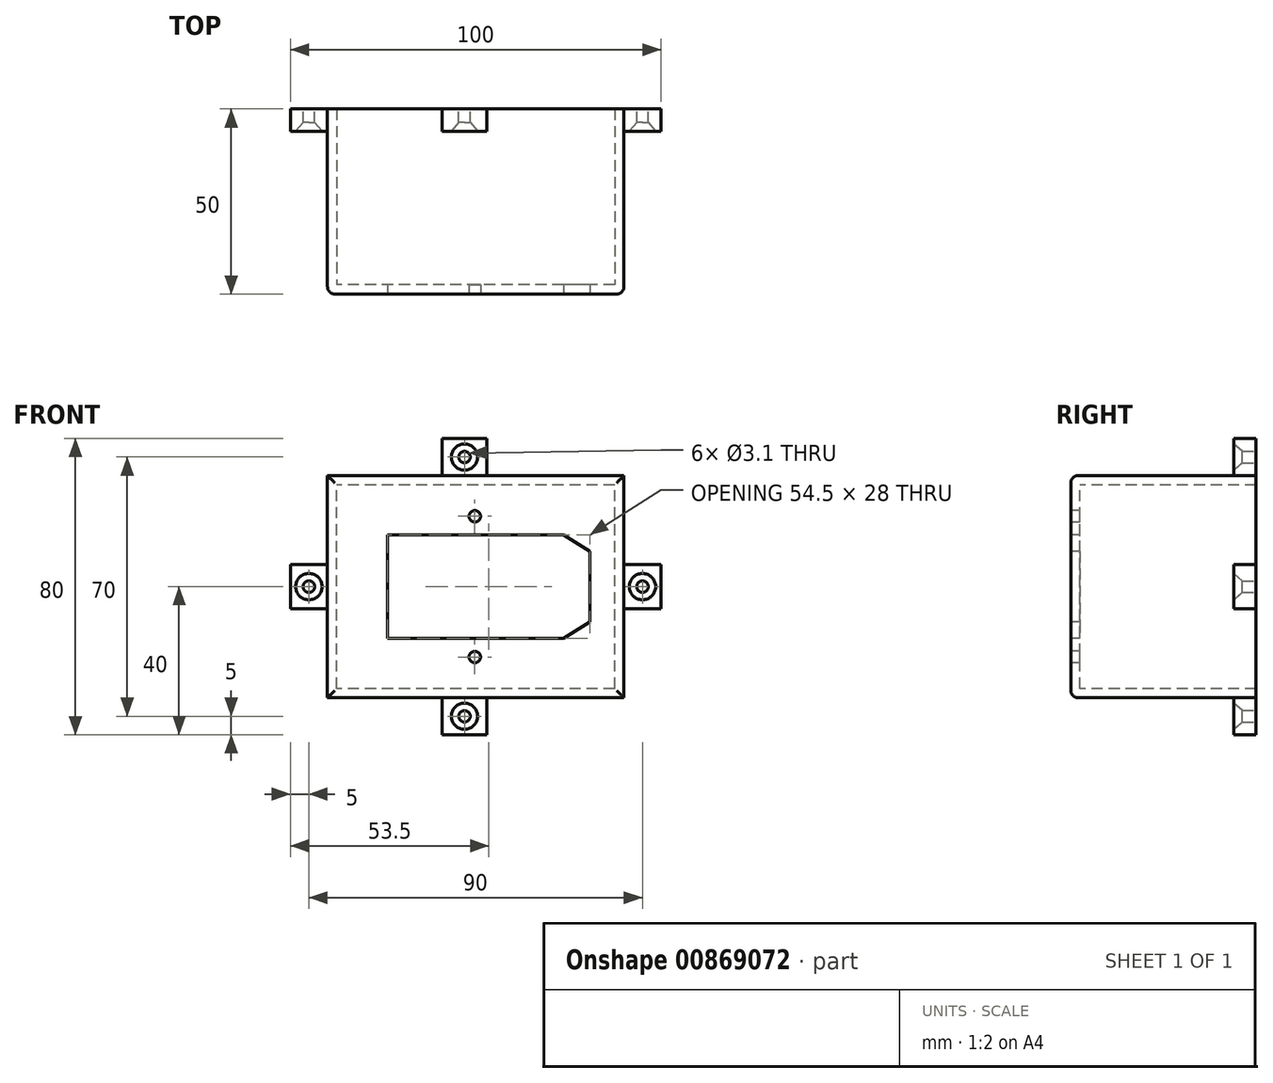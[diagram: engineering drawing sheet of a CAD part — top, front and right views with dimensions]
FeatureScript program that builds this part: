
annotation { "Feature Type Name" : "Feature", "Feature Type Description" : "" }
export const myFeature = defineFeature(function(context is Context, id is Id, definition is map)
    precondition{}
    {
        {
            var Q0;
            Q0=qCreatedBy(makeId("Front.planeOp"),FACE);
            var sketch = newSketch(context, id + "F0", { "sketchPlane" : qUnion([Q0])});
            skLineSegment(sketch, "E0.bottom", {"start": v(40, -30) * mm, "end": v(-40, -30) * mm});
            skLineSegment(sketch, "E0.top", {"start": v(40, 30) * mm, "end": v(-40, 30) * mm});
            skLineSegment(sketch, "E0.left", {"start": v(40, -30) * mm, "end": v(40, 30) * mm});
            skLineSegment(sketch, "E0.right", {"start": v(-40, -30) * mm, "end": v(-40, 30) * mm});
            skPoint(sketch, "E0.middle", {"position": v(0, 0) * mm});
            skLineSegment(sketch, "E1.bottom", {"start": v(23.75, -14) * mm, "end": v(-23.75, -14) * mm});
            skLineSegment(sketch, "E1.top", {"start": v(23.75, 14) * mm, "end": v(-23.75, 14) * mm});
            skLineSegment(sketch, "E1.left", {"start": v(23.75, -14) * mm, "end": v(23.75, 14) * mm});
            skLineSegment(sketch, "E1.right", {"start": v(-23.75, -14) * mm, "end": v(-23.75, 14) * mm});
            skLineSegment(sketch, "E2", {"start": v(30.75, 9.5) * mm, "end": v(30.75, -9.5) * mm});
            skLineSegment(sketch, "E3", {"start": v(30.75, -9.5) * mm, "end": v(23.75, -14) * mm});
            skLineSegment(sketch, "E4", {"start": v(30.75, 9.5) * mm, "end": v(23.75, 14) * mm});
            skLineSegment(sketch, "E5.0", {"start": v(37.5, -27.5) * mm, "end": v(-37.5, -27.5) * mm});
            skLineSegment(sketch, "E5.1", {"start": v(37.5, -27.5) * mm, "end": v(37.5, 27.5) * mm});
            skLineSegment(sketch, "E5.2", {"start": v(37.5, 27.5) * mm, "end": v(-37.5, 27.5) * mm});
            skLineSegment(sketch, "E5.3", {"start": v(-37.5, -27.5) * mm, "end": v(-37.5, 27.5) * mm});
            skCircle(sketch, "E6", {"center": v(-0.25, 19) * mm, "radius": 1.55 * mm});
            skPoint(sketch, "E6.centerSnap0", {"position": v(0, 14) * mm});
            skCircle(sketch, "E7.MirrorC", {"center": v(-0.25, -19) * mm, "radius": 1.55 * mm});
            skSolve(sketch);
        }
        {
            var Q0;
            Q0 = qSketchRegion(id + "F0", true);
            extrude(context, id + "F1", {"entities" : qUnion([Q0]), "oppositeDirection" : true, "depth" : 50 * mm, "offsetDistance" : 25 * mm});
        }
        {
            var Q0;
            Q0=makeQuery(id+"F0.imprint","IMPRINT",FACE,{"disambiguationData":[TD([[makeQuery(id+"F0.imprint","IMPRINT",EDGE,{"derivedFrom":sQuery(id+"F0.wireOp",EDGE,"E1.bottom")}),1.0]])]});
            extrude(context, id + "F2", {"entities" : qUnion([Q0]), "operationType" : NewBodyOperationType.ADD, "oppositeDirection" : true, "depth" : 2.5 * mm, "offsetDistance" : 25 * mm});
        }
        {
            var Q0;
            Q0=makeQuery(id+"F1.opExtrude","CAP_FACE",FACE,{"disambiguationData":[OSD([sQuery(id+"F0.wireOp",EDGE,"E0.bottom"),sQuery(id+"F0.wireOp",EDGE,"E0.top"),sQuery(id+"F0.wireOp",EDGE,"E0.left"),sQuery(id+"F0.wireOp",EDGE,"E0.right"),sQuery(id+"F0.wireOp",EDGE,"E5.0"),sQuery(id+"F0.wireOp",EDGE,"E5.1"),sQuery(id+"F0.wireOp",EDGE,"E5.2"),sQuery(id+"F0.wireOp",EDGE,"E5.3")])],"isStart":false});
            var sketch = newSketch(context, id + "F3", { "sketchPlane" : qUnion([Q0])});
            skLineSegment(sketch, "E8.bottom", {"start": v(40, -6) * mm, "end": v(50, -6) * mm});
            skLineSegment(sketch, "E8.top", {"start": v(40, 6) * mm, "end": v(50, 6) * mm});
            skLineSegment(sketch, "E8.left", {"start": v(40, -6) * mm, "end": v(40, 6) * mm});
            skLineSegment(sketch, "E8.right", {"start": v(50, -6) * mm, "end": v(50, 6) * mm});
            skCircle(sketch, "E9", {"center": v(45, 0) * mm, "radius": 1.55 * mm});
            skLineSegment(sketch, "E10.MirrorCS", {"start": v(-50, -6) * mm, "end": v(-50, 6) * mm});
            skCircle(sketch, "E11.MirrorC", {"center": v(-45, 0) * mm, "radius": 1.55 * mm});
            skLineSegment(sketch, "E12.MirrorCS", {"start": v(-40, -6) * mm, "end": v(-50, -6) * mm});
            skLineSegment(sketch, "E13.MirrorCS", {"start": v(-40, -6) * mm, "end": v(-40, 6) * mm});
            skLineSegment(sketch, "E14.MirrorCS", {"start": v(-40, 6) * mm, "end": v(-50, 6) * mm});
            skLineSegment(sketch, "E15.bottom", {"start": v(-2.98, -40) * mm, "end": v(9.02, -40) * mm});
            skLineSegment(sketch, "E15.top", {"start": v(-2.98, -30) * mm, "end": v(9.02, -30) * mm});
            skLineSegment(sketch, "E15.left", {"start": v(-2.98, -40) * mm, "end": v(-2.98, -30) * mm});
            skLineSegment(sketch, "E15.right", {"start": v(9.02, -40) * mm, "end": v(9.02, -30) * mm});
            skCircle(sketch, "E16", {"center": v(3.02, -35) * mm, "radius": 1.55 * mm});
            skLineSegment(sketch, "E17.MirrorCS", {"start": v(9.02, 40) * mm, "end": v(9.02, 30) * mm});
            skLineSegment(sketch, "E18.MirrorCS", {"start": v(-2.98, 40) * mm, "end": v(-2.98, 30) * mm});
            skLineSegment(sketch, "E19.MirrorCS", {"start": v(-2.98, 40) * mm, "end": v(9.02, 40) * mm});
            skLineSegment(sketch, "E20.MirrorCS", {"start": v(-2.98, 30) * mm, "end": v(9.02, 30) * mm});
            skCircle(sketch, "E21.MirrorC", {"center": v(3.02, 35) * mm, "radius": 1.55 * mm});
            skSolve(sketch);
        }
        {
            var Q0;
            Q0=makeQuery(id+"F3.imprint","IMPRINT",FACE,{"disambiguationData":[TD([[makeQuery(id+"F3.imprint","IMPRINT",EDGE,{"derivedFrom":sQuery(id+"F3.wireOp",EDGE,"E8.bottom")}),1.0]])]});
            var Q1;
            Q1=makeQuery(id+"F3.imprint","IMPRINT",FACE,{"disambiguationData":[TD([[makeQuery(id+"F3.imprint","IMPRINT",EDGE,{"derivedFrom":sQuery(id+"F3.wireOp",EDGE,"E15.bottom")}),1.0]])]});
            var Q2;
            Q2=makeQuery(id+"F3.imprint","IMPRINT",FACE,{"disambiguationData":[TD([[makeQuery(id+"F3.imprint","IMPRINT",EDGE,{"derivedFrom":sQuery(id+"F3.wireOp",EDGE,"E13.MirrorCS")}),1.0]])]});
            var Q3;
            Q3=makeQuery(id+"F3.imprint","IMPRINT",FACE,{"disambiguationData":[TD([[makeQuery(id+"F3.imprint","IMPRINT",EDGE,{"derivedFrom":sQuery(id+"F3.wireOp",EDGE,"E17.MirrorCS")}),-1.0]])]});
            extrude(context, id + "F4", {"entities" : qUnion([Q0, Q1, Q2, Q3]), "operationType" : NewBodyOperationType.ADD, "oppositeDirection" : true, "depth" : 6 * mm, "offsetDistance" : 25 * mm});
        }
        {
            var Q0;
            Q0=makeQuery(id+"F1.opExtrude","CAP_EDGE",EDGE,{"disambiguationData":[OSD([sQuery(id+"F0.wireOp",EDGE,"E0.left")])],"isStart":true});
            var Q1;
            Q1=makeQuery(id+"F1.opExtrude","CAP_EDGE",EDGE,{"disambiguationData":[OSD([sQuery(id+"F0.wireOp",EDGE,"E0.right")])],"isStart":true});
            var Q2;
            Q2=makeQuery(id+"F1.opExtrude","CAP_EDGE",EDGE,{"disambiguationData":[OSD([sQuery(id+"F0.wireOp",EDGE,"E0.top")])],"isStart":true});
            var Q3;
            Q3=makeQuery(id+"F1.opExtrude","CAP_EDGE",EDGE,{"disambiguationData":[OSD([sQuery(id+"F0.wireOp",EDGE,"E0.bottom")])],"isStart":true});
            fillet(context, id + "F5", {"entities" : qUnion([Q0, Q1, Q2, Q3]), "radius" : 2 * mm, "tangentPropagation" : true, "allowEdgeOverflow" : false});
        }
        {
            var Q0;
            Q0=makeQuery(id+"F4.opExtrude","CAP_FACE",FACE,{"disambiguationData":[OSD([sQuery(id+"F3.wireOp",EDGE,"E15.bottom"),sQuery(id+"F3.wireOp",EDGE,"E15.top"),sQuery(id+"F3.wireOp",EDGE,"E15.left"),sQuery(id+"F3.wireOp",EDGE,"E15.right"),sQuery(id+"F3.wireOp",EDGE,"E16")])],"isStart":false});
            var sketch = newSketch(context, id + "F6", { "sketchPlane" : qUnion([Q0])});
            skPoint(sketch, "E22", {"position": v(-3.02, -35) * mm});
            skSolve(sketch);
        }
        {
            var Q0;
            Q0=makeQuery(id+"F4.opExtrude","CAP_FACE",FACE,{"disambiguationData":[OSD([sQuery(id+"F3.wireOp",EDGE,"E17.MirrorCS"),sQuery(id+"F3.wireOp",EDGE,"E18.MirrorCS"),sQuery(id+"F3.wireOp",EDGE,"E19.MirrorCS"),sQuery(id+"F3.wireOp",EDGE,"E20.MirrorCS"),sQuery(id+"F3.wireOp",EDGE,"E21.MirrorC")])],"isStart":false});
            var sketch = newSketch(context, id + "F7", { "sketchPlane" : qUnion([Q0])});
            skPoint(sketch, "E23", {"position": v(-3.02, 35) * mm});
            skSolve(sketch);
        }
        {
            var Q0;
            Q0=makeQuery(id+"F4.opExtrude","CAP_FACE",FACE,{"disambiguationData":[OSD([sQuery(id+"F3.wireOp",EDGE,"E13.MirrorCS"),sQuery(id+"F3.wireOp",EDGE,"E11.MirrorC"),sQuery(id+"F3.wireOp",EDGE,"E10.MirrorCS"),sQuery(id+"F3.wireOp",EDGE,"E14.MirrorCS"),sQuery(id+"F3.wireOp",EDGE,"E12.MirrorCS")])],"isStart":false});
            var sketch = newSketch(context, id + "F8", { "sketchPlane" : qUnion([Q0])});
            skPoint(sketch, "E24", {"position": v(45, 0) * mm});
            skSolve(sketch);
        }
        {
            var Q0;
            Q0=makeQuery(id+"F4.opExtrude","CAP_FACE",FACE,{"disambiguationData":[OSD([sQuery(id+"F3.wireOp",EDGE,"E8.bottom"),sQuery(id+"F3.wireOp",EDGE,"E8.top"),sQuery(id+"F3.wireOp",EDGE,"E8.left"),sQuery(id+"F3.wireOp",EDGE,"E8.right"),sQuery(id+"F3.wireOp",EDGE,"E9")])],"isStart":false});
            var sketch = newSketch(context, id + "F9", { "sketchPlane" : qUnion([Q0])});
            skPoint(sketch, "E25", {"position": v(-45, 0) * mm});
            skSolve(sketch);
        }
        {
            var Q0;
            Q0=sQuery(id+"F6.wireOp",VERTEX,"E22");
            var Q1;
            Q1=sQuery(id+"F7.wireOp",VERTEX,"E23");
            var Q2;
            Q2=sQuery(id+"F9.wireOp",VERTEX,"E25");
            var Q3;
            Q3=sQuery(id+"F8.wireOp",VERTEX,"E24");
            var Q4;
            Q4=makeQuery(id+"F1.opExtrude","SWEPT_BODY",BODY,{"disambiguationData":[OSD([sQuery(id+"F0.wireOp",EDGE,"E0.bottom"),sQuery(id+"F0.wireOp",EDGE,"E0.top"),sQuery(id+"F0.wireOp",EDGE,"E0.left"),sQuery(id+"F0.wireOp",EDGE,"E0.right"),sQuery(id+"F0.wireOp",EDGE,"E5.0"),sQuery(id+"F0.wireOp",EDGE,"E5.1"),sQuery(id+"F0.wireOp",EDGE,"E5.2"),sQuery(id+"F0.wireOp",EDGE,"E5.3")])]});
            hole(context, id + "F10", {"style" : HoleStyle.C_SINK, "endStyle" : HoleEndStyle.THROUGH, "holeDiameter" : 3.1 * mm, "cSinkDiameter" : 7.1 * mm, "cSinkAngle" : 82 * degree, "majorDiameter" : 5 * mm, "isTappedThrough" : true, "tappedDepth" : 12 * mm, "tapClearance" : 3, "locations" : qUnion([Q0, Q1, Q2, Q3]), "scope" : qUnion([Q4])});
        }
    });
